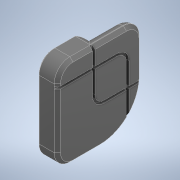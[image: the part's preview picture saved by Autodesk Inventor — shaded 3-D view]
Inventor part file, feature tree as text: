
AUTODESK INVENTOR PART (.ipt)
format: ipt  version: 2021 (Build 250183000, 183)  size: 367,616 bytes
history: native  units: mm
features: delete_face x6, chamfer x5, fillet x4, direct_edit x2, projected_geometry x2, move_body x2, sketch x1, extrude x1
ambient origin geometry x8: Origin, YZ Plane, XZ Plane, XY Plane, X Axis, Y Axis, Z Axis, Center Point
bodies: Volumenkörper2 (feature_tree), Volumenkörper1 (feature_tree)
feature tree (23):
  sketch  "Skizze1"  dims[d1=7.4mm d2=4.7mm d3=4.7mm d4=0.0mm d5=15.0mm d6=0.0mm d7=0.0mm d8=1.5mm d9=0.0mm d10=0.0mm d11=-11.0mm d12=13.5mm d14=1.0mm d15=2.0mm d16=45.0deg d17=2.6mm d18=5.0mm d19=1.0mm d20=2.0mm d21=45.0deg d22=4.8mm d23=0.0mm d24=0.4mm d25=2.0mm d26=45.0deg d27=2.4mm d28=2.0mm d29=45.0deg d30=2.0mm d31=0.4mm d32=2.0mm d33=45.0deg]
  delete_face  "Fläche löschen1"
  delete_face  "Fläche löschen2"
  direct_edit  "Direktbearbeitung1"
  delete_face  "Fläche löschen3"
  delete_face  "Fläche löschen4"
  direct_edit  "Direktbearbeitung2"
  delete_face  "Fläche löschen5"
  fillet  "Rundung1"  Radius=2.1mm
  delete_face  "Fläche löschen6"
  chamfer  "Fase1"  Distance=4.7mm
  fillet  "Rundung3"  Radius=4.7mm
  fillet  "Rundung4"  [1 undecoded]
  chamfer  "Fase2"  Distance=15.0mm
  extrude  "Extrusion1"  Depth=2.0mm TaperAngle=0.0deg
  chamfer  "Fase3"  [1 undecoded]
  chamfer  "Fase4"  Distance=13.5mm
  fillet  "Rundung5"  Radius=1.0mm
  chamfer  "Fase5"  Distance=2.6mm
  projected_geometry  "Projizierte Kontur1"
  projected_geometry  "Projizierte Kontur2"
  move_body  "Verschieben1"
  move_body  "Verschieben2"
note: 2 required parameter values undecoded (feature->parameter linkage not recoverable at this tier; creation-order binding heuristic only, values carry confidence <= 0.55)
